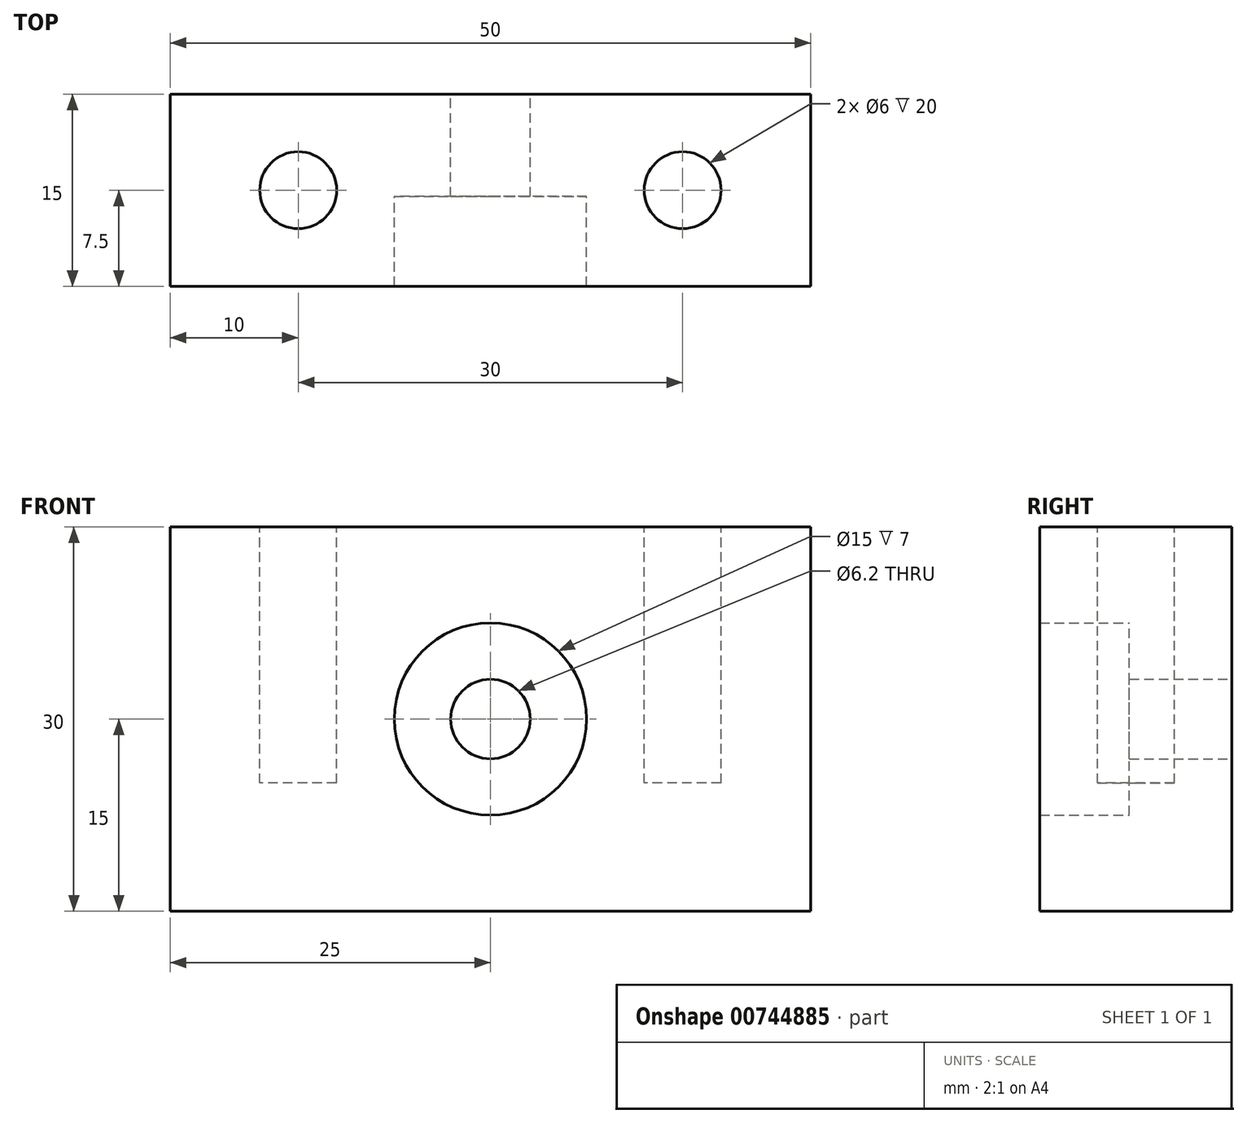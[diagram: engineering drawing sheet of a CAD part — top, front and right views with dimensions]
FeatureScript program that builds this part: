
annotation { "Feature Type Name" : "Feature", "Feature Type Description" : "" }
export const myFeature = defineFeature(function(context is Context, id is Id, definition is map)
    precondition{}
    {
        {
            var Q0;
            Q0=qCreatedBy(makeId("Front.planeOp"),FACE);
            var sketch = newSketch(context, id + "F0", { "sketchPlane" : qUnion([Q0])});
            skLineSegment(sketch, "E0.bottom", {"start": v(25, -15) * mm, "end": v(-25, -15) * mm});
            skLineSegment(sketch, "E0.top", {"start": v(25, 15) * mm, "end": v(-25, 15) * mm});
            skLineSegment(sketch, "E0.left", {"start": v(25, -15) * mm, "end": v(25, 15) * mm});
            skLineSegment(sketch, "E0.right", {"start": v(-25, -15) * mm, "end": v(-25, 15) * mm});
            skPoint(sketch, "E0.middle", {"position": v(0, 0) * mm});
            skCircle(sketch, "E1", {"center": v(0, 0) * mm, "radius": 3.1 * mm});
            skCircle(sketch, "E2", {"center": v(0, 0) * mm, "radius": 7.5 * mm});
            skSolve(sketch);
        }
        {
            var Q0;
            Q0 = qSketchRegion(id + "F0", true);
            extrude(context, id + "F1", {"entities" : qUnion([Q0]), "depth" : 15 * mm, "offsetDistance" : 25 * mm});
        }
        {
            var Q0;
            Q0=makeQuery(id+"F0.imprint","IMPRINT",FACE,{"disambiguationData":[TD([[makeQuery(id+"F0.imprint","IMPRINT",EDGE,{"derivedFrom":sQuery(id+"F0.wireOp",EDGE,"E1")}),-1.0]])]});
            extrude(context, id + "F2", {"entities" : qUnion([Q0]), "operationType" : NewBodyOperationType.ADD, "depth" : 8 * mm, "offsetDistance" : 25 * mm});
        }
        {
            var Q0;
            Q0=makeQuery(id+"F1.opExtrude","SWEPT_FACE",FACE,{"disambiguationData":[OSD([sQuery(id+"F0.wireOp",EDGE,"E0.top")])]});
            var sketch = newSketch(context, id + "F3", { "sketchPlane" : qUnion([Q0])});
            skCircle(sketch, "E3", {"center": v(-15, -7.5) * mm, "radius": 3 * mm});
            skPoint(sketch, "E3.centerSnap0", {"position": v(-25, -7.5) * mm});
            skCircle(sketch, "E4.MirrorC", {"center": v(15, -7.5) * mm, "radius": 3 * mm});
            skSolve(sketch);
        }
        {
            var Q0;
            Q0 = qSketchRegion(id + "F3", true);
            extrude(context, id + "F4", {"entities" : qUnion([Q0]), "operationType" : NewBodyOperationType.REMOVE, "oppositeDirection" : true, "depth" : 20 * mm, "offsetDistance" : 25 * mm});
        }
    });
